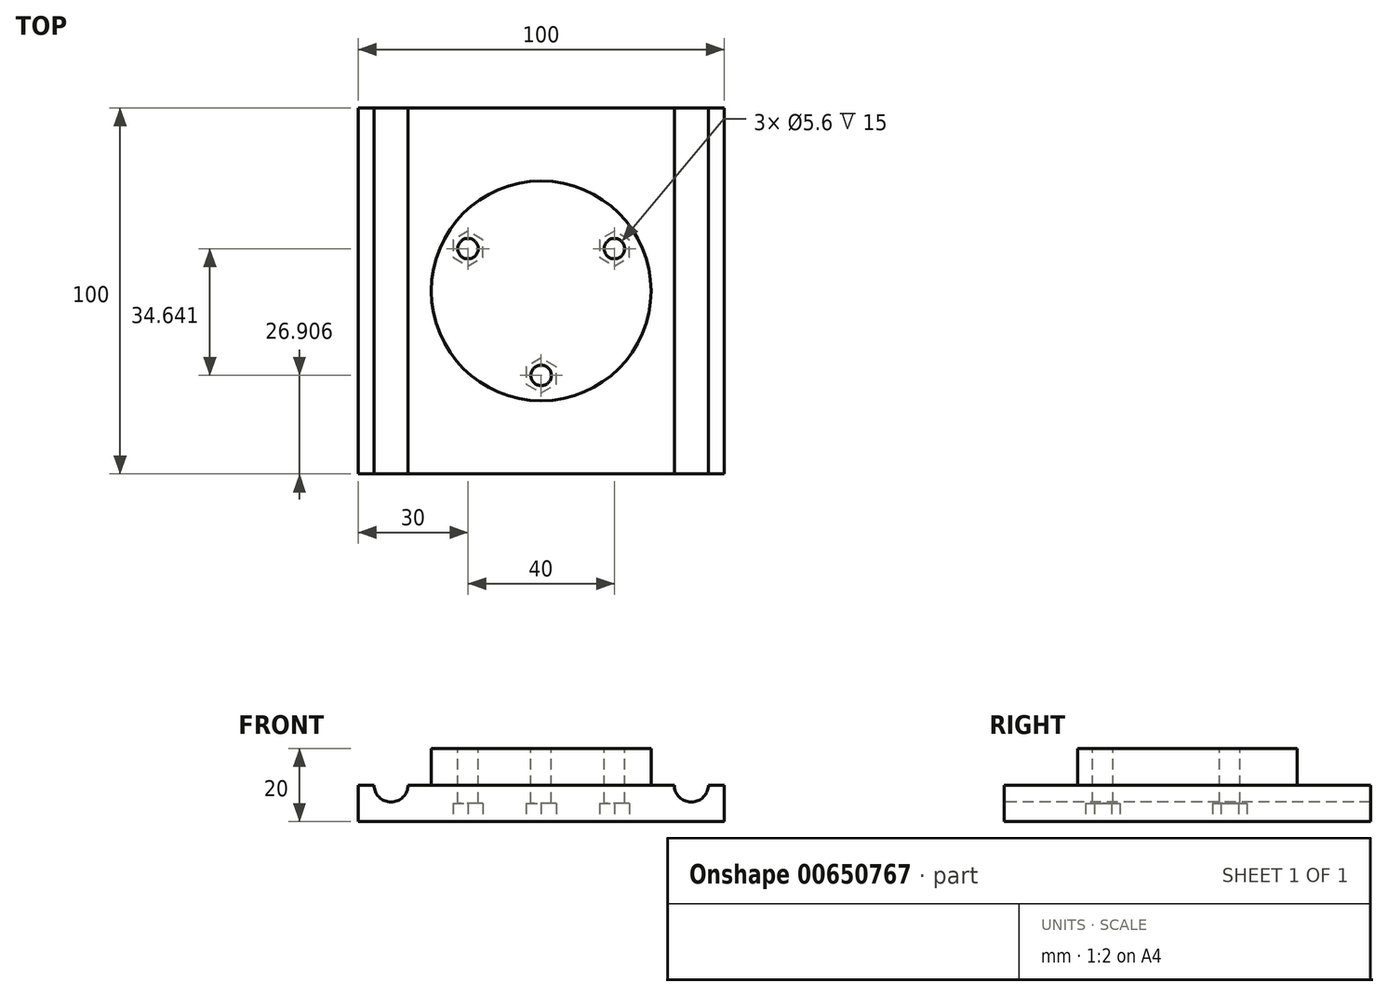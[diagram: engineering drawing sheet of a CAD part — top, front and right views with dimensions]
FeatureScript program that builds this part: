
annotation { "Feature Type Name" : "Feature", "Feature Type Description" : "" }
export const myFeature = defineFeature(function(context is Context, id is Id, definition is map)
    precondition{}
    {
        {
            var Q0;
            Q0=qCreatedBy(makeId("Top.planeOp"),FACE);
            var sketch = newSketch(context, id + "F0", { "sketchPlane" : qUnion([Q0])});
            skLineSegment(sketch, "E0.bottom", {"start": v(50, -50) * mm, "end": v(-50, -50) * mm});
            skLineSegment(sketch, "E0.top", {"start": v(50, 50) * mm, "end": v(-50, 50) * mm});
            skLineSegment(sketch, "E0.left", {"start": v(50, -50) * mm, "end": v(50, 50) * mm});
            skLineSegment(sketch, "E0.right", {"start": v(-50, -50) * mm, "end": v(-50, 50) * mm});
            skPoint(sketch, "E0.middle", {"position": v(0, 0) * mm});
            skSolve(sketch);
        }
        {
            var Q0;
            Q0 = qSketchRegion(id + "F0", true);
            extrude(context, id + "F1", {"entities" : qUnion([Q0]), "depth" : 10 * mm, "offsetDistance" : 25 * mm});
        }
        {
            var Q0;
            Q0=makeQuery(id+"F1.opExtrude","SWEPT_FACE",FACE,{"disambiguationData":[OSD([sQuery(id+"F0.wireOp",EDGE,"E0.bottom")])]});
            var sketch = newSketch(context, id + "F2", { "sketchPlane" : qUnion([Q0])});
            skPoint(sketch, "E1", {"position": v(-41, 10) * mm});
            skPoint(sketch, "E2", {"position": v(41, 10) * mm});
            skCircle(sketch, "E3", {"center": v(-41, 10) * mm, "radius": 4.65 * mm});
            skCircle(sketch, "E4", {"center": v(41, 10) * mm, "radius": 4.65 * mm});
            skSolve(sketch);
        }
        {
            var Q0;
            Q0 = qSketchRegion(id + "F2", true);
            extrude(context, id + "F3", {"entities" : qUnion([Q0]), "operationType" : NewBodyOperationType.REMOVE, "endBound" : BoundingType.THROUGH_ALL, "oppositeDirection" : true, "depth" : 25 * mm, "offsetDistance" : 25 * mm});
        }
        {
            var Q0;
            {var subQ0=sQuery(id+"F0.wireOp",EDGE,"E0.bottom");var subQ1=sQuery(id+"F0.wireOp",EDGE,"E0.top");Q0=makeQuery(id+"F3.boolean.opBoolean","SPLIT",FACE,{"disambiguationData":[TD([makeQuery(id+"F1.opExtrude","SWEPT_FACE",FACE,{"disambiguationData":[OSD([subQ0])]}),makeQuery(id+"F1.opExtrude","SWEPT_FACE",FACE,{"disambiguationData":[OSD([subQ1])]}),makeQuery(id+"F3.opExtrude","SWEPT_FACE",FACE,{"disambiguationData":[OSD([sQuery(id+"F2.wireOp",EDGE,"E3")])]}),makeQuery(id+"F3.opExtrude","SWEPT_FACE",FACE,{"disambiguationData":[OSD([sQuery(id+"F2.wireOp",EDGE,"E4")])]})])],"derivedFrom":makeQuery(id+"F1.opExtrude","CAP_FACE",FACE,{"disambiguationData":[OSD([subQ0,subQ1,sQuery(id+"F0.wireOp",EDGE,"E0.left"),sQuery(id+"F0.wireOp",EDGE,"E0.right")])],"isStart":false})});}
            var sketch = newSketch(context, id + "F4", { "sketchPlane" : qUnion([Q0])});
            skCircle(sketch, "E5", {"center": v(0, 0) * mm, "radius": 30 * mm});
            skSolve(sketch);
        }
        {
            var Q0;
            Q0 = qSketchRegion(id + "F4", true);
            extrude(context, id + "F5", {"entities" : qUnion([Q0]), "operationType" : NewBodyOperationType.ADD, "depth" : 10 * mm, "offsetDistance" : 25 * mm});
        }
        {
            var Q0;
            Q0=makeQuery(id+"F5.opExtrude","CAP_FACE",FACE,{"disambiguationData":[OSD([sQuery(id+"F4.wireOp",EDGE,"E5")])],"isStart":false});
            var sketch = newSketch(context, id + "F6", { "sketchPlane" : qUnion([Q0])});
            skCircle(sketch, "E6.cCircle", {"center": v(0, 0) * mm, "radius": 11.55 * mm, "construction": true});
            skLineSegment(sketch, "E6.0", {"start": v(20, 11.55) * mm, "end": v(0, -23.1) * mm});
            skLineSegment(sketch, "E6.1", {"start": v(0, -23.1) * mm, "end": v(-20, 11.55) * mm});
            skLineSegment(sketch, "E6.2", {"start": v(-20, 11.55) * mm, "end": v(20, 11.55) * mm});
            skPoint(sketch, "E6.0.midPoint", {"position": v(10, -5.77) * mm});
            skPoint(sketch, "E7", {"position": v(-20, 11.55) * mm});
            skPoint(sketch, "E8", {"position": v(20, 11.55) * mm});
            skPoint(sketch, "E9", {"position": v(0, -23.1) * mm});
            skCircle(sketch, "E10", {"center": v(-20, 11.55) * mm, "radius": 2.8 * mm});
            skCircle(sketch, "E11", {"center": v(20, 11.55) * mm, "radius": 2.8 * mm});
            skCircle(sketch, "E12", {"center": v(0, -23.1) * mm, "radius": 2.8 * mm});
            skSolve(sketch);
        }
        {
            var Q0;
            {var subQ0=sQuery(id+"F6.wireOp",EDGE,"E6.2");var subQ1=sQuery(id+"F6.wireOp",EDGE,"E6.1");var subQ2=makeQuery(id+"F6.imprint","INTERSECT",VERTEX,{"derivedFrom":[subQ1,subQ0]});Q0=makeQuery(id+"F6.imprint","IMPRINT",FACE,{"disambiguationData":[TD([[makeQuery(id+"F6.imprint","IMPRINT",EDGE,{"disambiguationData":[TD([[subQ2,1.0]])],"derivedFrom":subQ1}),-1.0]])]});}
            var Q1;
            {var subQ0=sQuery(id+"F6.wireOp",EDGE,"E6.2");var subQ1=sQuery(id+"F6.wireOp",EDGE,"E6.1");var subQ2=makeQuery(id+"F6.imprint","INTERSECT",VERTEX,{"derivedFrom":[subQ1,subQ0]});Q1=makeQuery(id+"F6.imprint","IMPRINT",FACE,{"disambiguationData":[TD([[makeQuery(id+"F6.imprint","IMPRINT",EDGE,{"disambiguationData":[TD([[subQ2,1.0]])],"derivedFrom":subQ1}),1.0]])]});}
            var Q2;
            {var subQ0=sQuery(id+"F6.wireOp",EDGE,"E6.2");var subQ1=sQuery(id+"F6.wireOp",EDGE,"E6.0");var subQ2=makeQuery(id+"F6.imprint","INTERSECT",VERTEX,{"derivedFrom":[subQ1,subQ0]});Q2=makeQuery(id+"F6.imprint","IMPRINT",FACE,{"disambiguationData":[TD([[makeQuery(id+"F6.imprint","IMPRINT",EDGE,{"disambiguationData":[TD([[subQ2,-1.0]])],"derivedFrom":subQ1}),-1.0]])]});}
            var Q3;
            {var subQ0=sQuery(id+"F6.wireOp",EDGE,"E6.2");var subQ1=sQuery(id+"F6.wireOp",EDGE,"E6.0");var subQ2=makeQuery(id+"F6.imprint","INTERSECT",VERTEX,{"derivedFrom":[subQ1,subQ0]});Q3=makeQuery(id+"F6.imprint","IMPRINT",FACE,{"disambiguationData":[TD([[makeQuery(id+"F6.imprint","IMPRINT",EDGE,{"disambiguationData":[TD([[subQ2,-1.0]])],"derivedFrom":subQ1}),1.0]])]});}
            var Q4;
            {var subQ0=sQuery(id+"F6.wireOp",EDGE,"E6.1");var subQ1=sQuery(id+"F6.wireOp",EDGE,"E6.0");var subQ2=makeQuery(id+"F6.imprint","INTERSECT",VERTEX,{"derivedFrom":[subQ1,subQ0]});Q4=makeQuery(id+"F6.imprint","IMPRINT",FACE,{"disambiguationData":[TD([[makeQuery(id+"F6.imprint","IMPRINT",EDGE,{"disambiguationData":[TD([[subQ2,1.0]])],"derivedFrom":subQ1}),-1.0]])]});}
            var Q5;
            {var subQ0=sQuery(id+"F6.wireOp",EDGE,"E6.1");var subQ1=sQuery(id+"F6.wireOp",EDGE,"E6.0");var subQ2=makeQuery(id+"F6.imprint","INTERSECT",VERTEX,{"derivedFrom":[subQ1,subQ0]});Q5=makeQuery(id+"F6.imprint","IMPRINT",FACE,{"disambiguationData":[TD([[makeQuery(id+"F6.imprint","IMPRINT",EDGE,{"disambiguationData":[TD([[subQ2,1.0]])],"derivedFrom":subQ1}),1.0]])]});}
            extrude(context, id + "F7", {"entities" : qUnion([Q0, Q1, Q2, Q3, Q4, Q5]), "operationType" : NewBodyOperationType.REMOVE, "endBound" : BoundingType.THROUGH_ALL, "oppositeDirection" : true, "depth" : 25 * mm, "offsetDistance" : 25 * mm});
        }
        {
            var Q0;
            Q0=makeQuery(id+"F1.opExtrude","CAP_FACE",FACE,{"disambiguationData":[OSD([sQuery(id+"F0.wireOp",EDGE,"E0.bottom"),sQuery(id+"F0.wireOp",EDGE,"E0.top"),sQuery(id+"F0.wireOp",EDGE,"E0.left"),sQuery(id+"F0.wireOp",EDGE,"E0.right")])],"isStart":true});
            var sketch = newSketch(context, id + "F8", { "sketchPlane" : qUnion([Q0])});
            skPoint(sketch, "E13", {"position": v(0, 23.1) * mm});
            skPoint(sketch, "E14", {"position": v(-20, -11.55) * mm});
            skPoint(sketch, "E15", {"position": v(20, -11.55) * mm});
            skCircle(sketch, "E16.cCircle", {"center": v(0, 23.1) * mm, "radius": 4.1 * mm, "construction": true});
            skLineSegment(sketch, "E16.0", {"start": v(4.1, 20.73) * mm, "end": v(0, 18.36) * mm});
            skLineSegment(sketch, "E16.1", {"start": v(0, 18.36) * mm, "end": v(-4.1, 20.73) * mm});
            skLineSegment(sketch, "E16.2", {"start": v(-4.1, 20.73) * mm, "end": v(-4.1, 25.46) * mm});
            skLineSegment(sketch, "E16.3", {"start": v(-4.1, 25.46) * mm, "end": v(0, 27.83) * mm});
            skLineSegment(sketch, "E16.4", {"start": v(0, 27.83) * mm, "end": v(4.1, 25.46) * mm});
            skLineSegment(sketch, "E16.5", {"start": v(4.1, 25.46) * mm, "end": v(4.1, 20.73) * mm});
            skPoint(sketch, "E16.0.midPoint", {"position": v(2.05, 19.54) * mm});
            skCircle(sketch, "E17.cCircle", {"center": v(20, -11.55) * mm, "radius": 4.1 * mm, "construction": true});
            skLineSegment(sketch, "E17.0", {"start": v(24.1, -13.91) * mm, "end": v(20, -16.28) * mm});
            skLineSegment(sketch, "E17.1", {"start": v(20, -16.28) * mm, "end": v(15.9, -13.91) * mm});
            skLineSegment(sketch, "E17.2", {"start": v(15.9, -13.91) * mm, "end": v(15.9, -9.18) * mm});
            skLineSegment(sketch, "E17.3", {"start": v(15.9, -9.18) * mm, "end": v(20, -6.81) * mm});
            skLineSegment(sketch, "E17.4", {"start": v(20, -6.81) * mm, "end": v(24.1, -9.18) * mm});
            skLineSegment(sketch, "E17.5", {"start": v(24.1, -9.18) * mm, "end": v(24.1, -13.91) * mm});
            skPoint(sketch, "E17.0.midPoint", {"position": v(22.05, -15.1) * mm});
            skCircle(sketch, "E18.cCircle", {"center": v(-20, -11.55) * mm, "radius": 4.1 * mm, "construction": true});
            skLineSegment(sketch, "E18.0", {"start": v(-15.9, -13.91) * mm, "end": v(-20, -16.28) * mm});
            skLineSegment(sketch, "E18.1", {"start": v(-20, -16.28) * mm, "end": v(-24.1, -13.91) * mm});
            skLineSegment(sketch, "E18.2", {"start": v(-24.1, -13.91) * mm, "end": v(-24.1, -9.18) * mm});
            skLineSegment(sketch, "E18.3", {"start": v(-24.1, -9.18) * mm, "end": v(-20, -6.81) * mm});
            skLineSegment(sketch, "E18.4", {"start": v(-20, -6.81) * mm, "end": v(-15.9, -9.18) * mm});
            skLineSegment(sketch, "E18.5", {"start": v(-15.9, -9.18) * mm, "end": v(-15.9, -13.91) * mm});
            skPoint(sketch, "E18.0.midPoint", {"position": v(-17.95, -15.1) * mm});
            skSolve(sketch);
        }
        {
            var Q0;
            Q0=makeQuery(id+"F8.imprint","IMPRINT",FACE,{"disambiguationData":[TD([[makeQuery(id+"F8.imprint","IMPRINT",EDGE,{"derivedFrom":sQuery(id+"F8.wireOp",EDGE,"E16.0")}),-1.0]])]});
            var Q1;
            Q1=makeQuery(id+"F8.imprint","IMPRINT",FACE,{"disambiguationData":[TD([[makeQuery(id+"F8.imprint","IMPRINT",EDGE,{"derivedFrom":sQuery(id+"F8.wireOp",EDGE,"E18.0")}),-1.0]])]});
            var Q2;
            Q2=makeQuery(id+"F8.imprint","IMPRINT",FACE,{"disambiguationData":[TD([[makeQuery(id+"F8.imprint","IMPRINT",EDGE,{"derivedFrom":sQuery(id+"F8.wireOp",EDGE,"E17.0")}),-1.0]])]});
            extrude(context, id + "F9", {"entities" : qUnion([Q0, Q1, Q2]), "operationType" : NewBodyOperationType.REMOVE, "oppositeDirection" : true, "depth" : 5 * mm, "offsetDistance" : 25 * mm});
        }
    });
